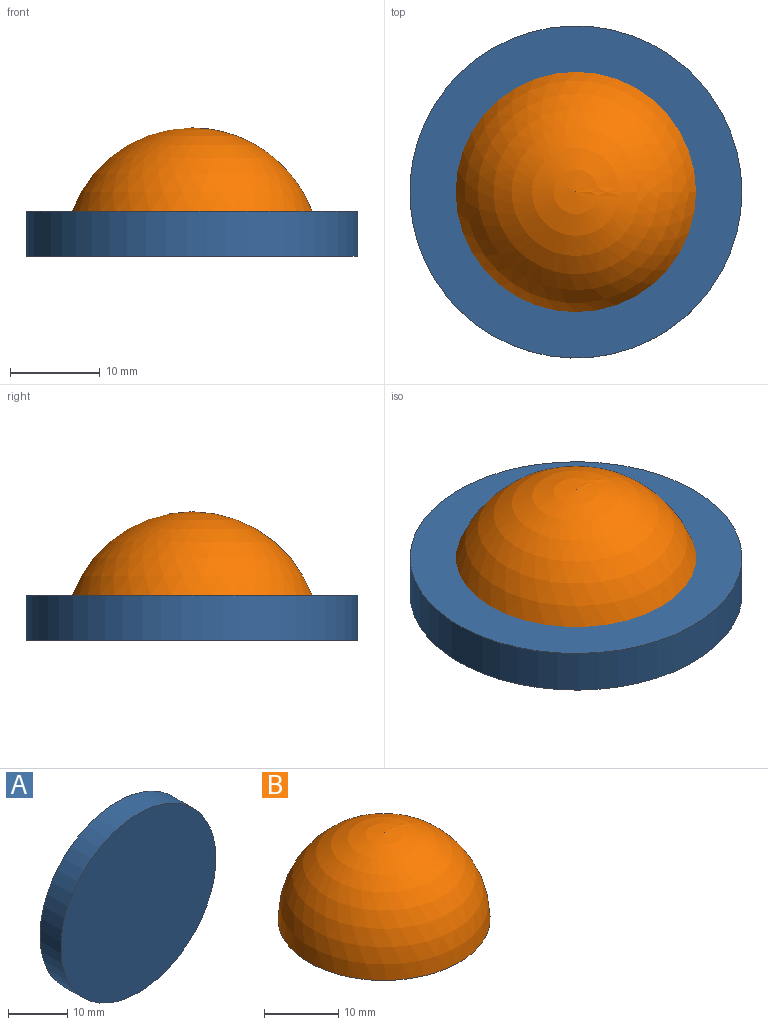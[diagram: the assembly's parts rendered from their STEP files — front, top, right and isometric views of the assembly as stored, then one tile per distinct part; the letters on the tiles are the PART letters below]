
ASSEMBLY  parts=2 mates=1
PART A: 3 faces, bbox 37x5x37 mm
  f0: cylinder r=18.5mm len=37.01mm, axis (0,1,0), area 581.3mm2, adj f1,f2
  f1: plane 37.01x37.01mm, normal (0,-1,0), area 1075.7mm2, adj f0
  f2: plane 37.01x37.01mm, normal (0,1,0), area 1075.7mm2, adj f0
PART B: 2 faces, bbox 28.6x28.6x14.3 mm
  f0: plane 28.61x28.61mm, normal (0,0,-1), area 642.9mm2, adj f1
  f1: sphere r=14.31mm, area 1285.8mm2, adj f0
PLACE A rot(axis=(1,0,0),90deg) t=(-31.75,-13.31,12.54)mm
PLACE B t=(-31.75,-13.31,7.54)mm
MATE fastened A.f0 <-> B.f0  axis (0,0,-1) through (-31.75,-13.31,7.54)mm
